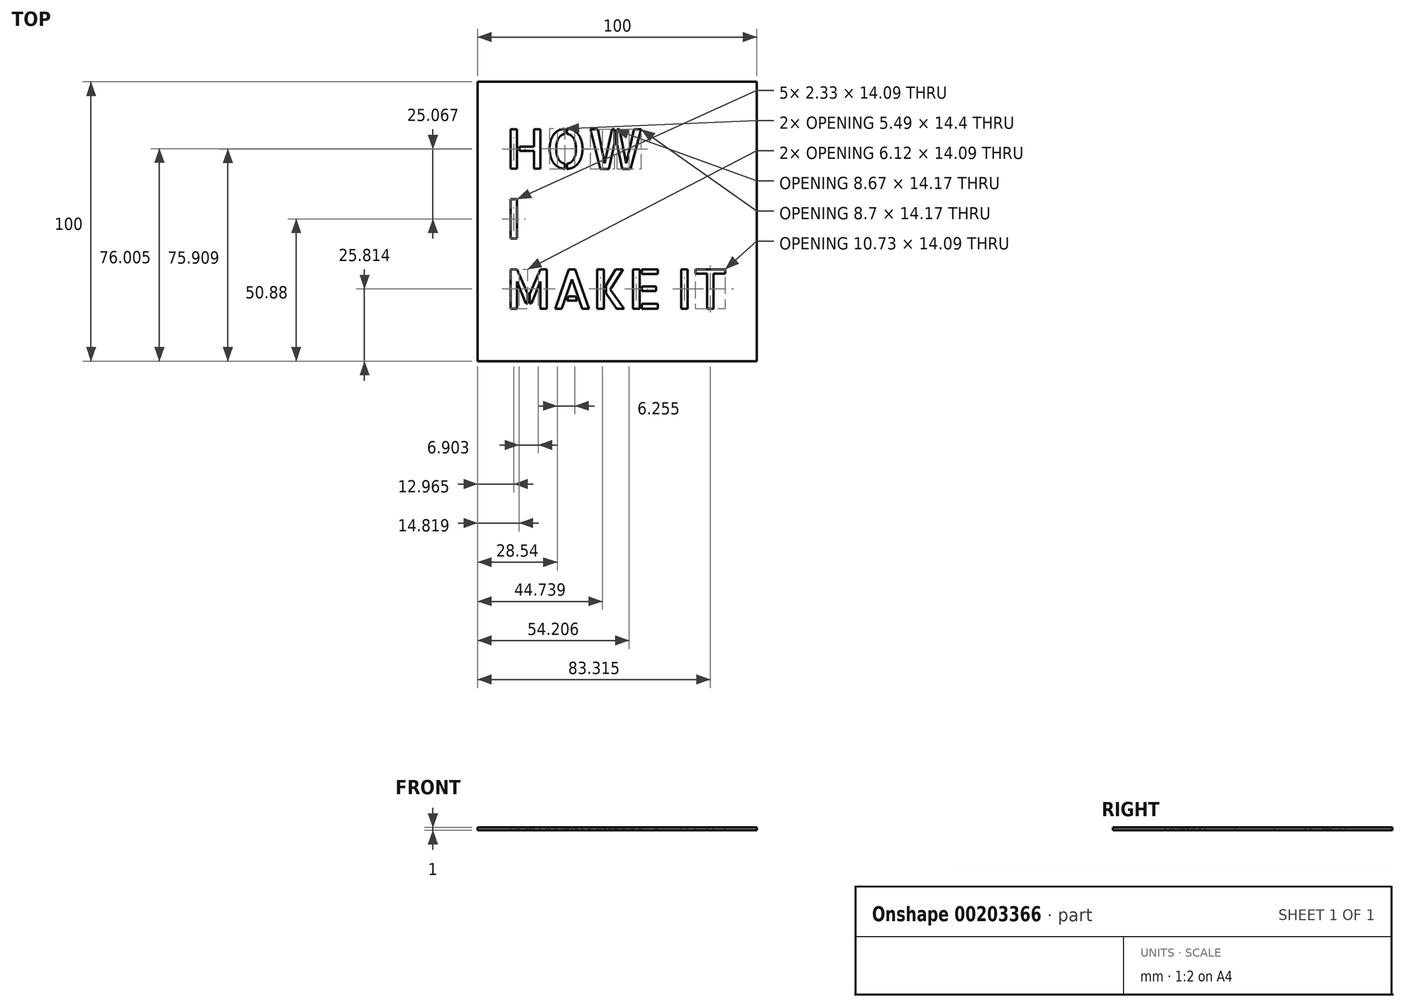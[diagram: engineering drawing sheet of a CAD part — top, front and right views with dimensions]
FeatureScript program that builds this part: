
annotation { "Feature Type Name" : "Feature", "Feature Type Description" : "" }
export const myFeature = defineFeature(function(context is Context, id is Id, definition is map)
    precondition{}
    {
        {
            var Q0;
            Q0=qCreatedBy(makeId("Top.planeOp"),FACE);
            var sketch = newSketch(context, id + "F0", { "sketchPlane" : qUnion([Q0])});
            skLineSegment(sketch, "E0.bottom", {"start": v(-50, 50) * mm, "end": v(50, 50) * mm});
            skLineSegment(sketch, "E0.top", {"start": v(-50, -50) * mm, "end": v(50, -50) * mm});
            skLineSegment(sketch, "E0.left", {"start": v(-50, 50) * mm, "end": v(-50, -50) * mm});
            skLineSegment(sketch, "E0.right", {"start": v(50, 50) * mm, "end": v(50, -50) * mm});
            skPoint(sketch, "E0.middle", {"position": v(0, 0) * mm});
            skSolve(sketch);
        }
        {
            var Q0;
            Q0 = qSketchRegion(id + "F0", true);
            extrude(context, id + "F1", {"entities" : qUnion([Q0]), "depth" : 1 * mm});
        }
        {
            var Q0;
            Q0=makeQuery(id+"F1.opExtrude","CAP_FACE",FACE,{"disambiguationData":[OSD([sQuery(id+"F0.wireOp",EDGE,"E0.bottom"),sQuery(id+"F0.wireOp",EDGE,"E0.top"),sQuery(id+"F0.wireOp",EDGE,"E0.left"),sQuery(id+"F0.wireOp",EDGE,"E0.right")])],"isStart":false});
            var sketch = newSketch(context, id + "F2", { "sketchPlane" : qUnion([Q0])});
            skText(sketch, "E1", { "text": "HOW\nI\nMAKE IT", "fontName": "AllertaStencil-Regular.ttf"});
            const initialGuessF2  = {"E1": [-0.04, 0.0189, 1, 0, 0.0141]};
            skSetInitialGuess(sketch, initialGuessF2);
            skSolve(sketch);
        }
        {
            var Q0;
            Q0 = qSketchRegion(id + "F2", true);
            extrude(context, id + "F3", {"entities" : qUnion([Q0]), "operationType" : NewBodyOperationType.REMOVE, "endBound" : BoundingType.THROUGH_ALL, "oppositeDirection" : true, "depth" : 49.5 * mm});
        }
    });
